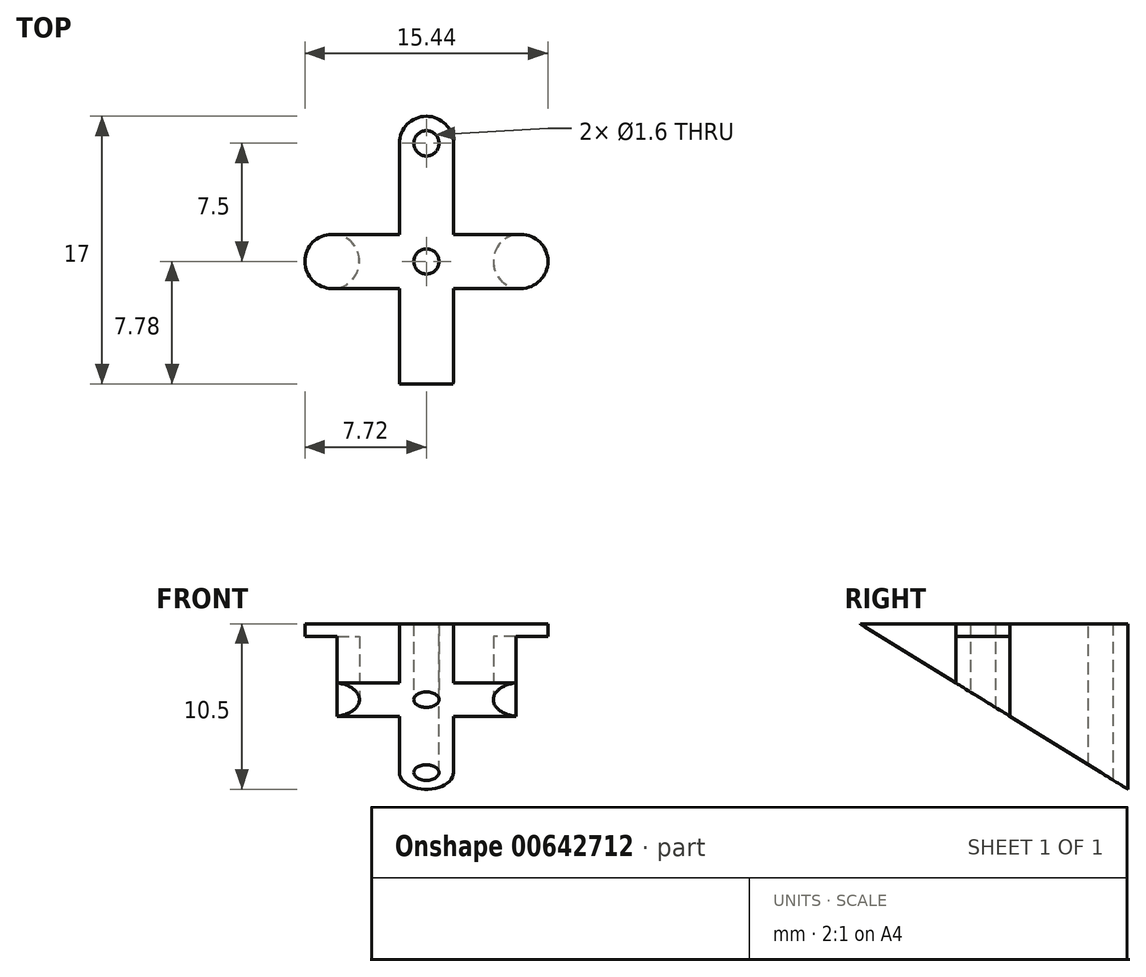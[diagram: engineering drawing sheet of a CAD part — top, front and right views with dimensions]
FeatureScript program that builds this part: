
annotation { "Feature Type Name" : "Feature", "Feature Type Description" : "" }
export const myFeature = defineFeature(function(context is Context, id is Id, definition is map)
    precondition{}
    {
        {
            var Q0;
            Q0=qCreatedBy(makeId("Top.planeOp"),FACE);
            var sketch = newSketch(context, id + "F0", { "sketchPlane" : qUnion([Q0])});
            skLineSegment(sketch, "E0.bottom", {"start": v(6, -1.72) * mm, "end": v(-6, -1.72) * mm});
            skLineSegment(sketch, "E0.top", {"start": v(6, 1.72) * mm, "end": v(-6, 1.72) * mm});
            skLineSegment(sketch, "E0.left", {"start": v(6, -1.72) * mm, "end": v(6, 1.72) * mm});
            skLineSegment(sketch, "E0.right", {"start": v(-6, -1.72) * mm, "end": v(-6, 1.72) * mm});
            skPoint(sketch, "E0.middle", {"position": v(0, 0) * mm});
            skLineSegment(sketch, "E1.bottom", {"start": v(1.72, -7.5) * mm, "end": v(-1.72, -7.5) * mm});
            skLineSegment(sketch, "E1.top", {"start": v(1.72, 7.5) * mm, "end": v(-1.72, 7.5) * mm});
            skLineSegment(sketch, "E1.left", {"start": v(1.72, -7.5) * mm, "end": v(1.72, 7.5) * mm});
            skLineSegment(sketch, "E1.right", {"start": v(-1.72, -7.5) * mm, "end": v(-1.72, 7.5) * mm});
            skArc(sketch, "E2", {"start": v(1.72, 7.5) * mm, "mid": v(0, 9.22) * mm, "end": v(-1.72, 7.5) * mm});
            skArc(sketch, "E3", {"start": v(6, -1.72) * mm, "mid": v(7.72, 0) * mm, "end": v(6, 1.72) * mm});
            skArc(sketch, "E4", {"start": v(-1.72, -7.5) * mm, "mid": v(0, -9.22) * mm, "end": v(1.72, -7.5) * mm});
            skArc(sketch, "E5", {"start": v(-6, 1.72) * mm, "mid": v(-7.72, 0) * mm, "end": v(-6, -1.72) * mm});
            skSolve(sketch);
        }
        {
            var Q0;
            Q0 = qSketchRegion(id + "F0", true);
            extrude(context, id + "F1", {"entities" : qUnion([Q0]), "depth" : 12 * mm, "offsetDistance" : 25 * mm});
        }
        {
            var Q0;
            Q0=qCreatedBy(makeId("Right.planeOp"),FACE);
            var sketch = newSketch(context, id + "F2", { "sketchPlane" : qUnion([Q0])});
            skLineSegment(sketch, "E6.0.0", {"start": v(7.5, 0) * mm, "end": v(9.22, 0) * mm, "construction": true});
            skLineSegment(sketch, "E6.0.1", {"start": v(7.5, 0) * mm, "end": v(7.5, 12) * mm});
            skLineSegment(sketch, "E6.0.2", {"start": v(7.5, 12) * mm, "end": v(9.22, 12) * mm, "construction": true});
            skLineSegment(sketch, "E6.0.3", {"start": v(7.5, 12) * mm, "end": v(7.5, 0) * mm, "construction": true});
            skLineSegment(sketch, "E7.0.0", {"start": v(-7.5, 0) * mm, "end": v(-9.22, 0) * mm, "construction": true});
            skLineSegment(sketch, "E7.0.1", {"start": v(-7.5, 0) * mm, "end": v(-7.5, 12) * mm});
            skLineSegment(sketch, "E7.0.2", {"start": v(-7.5, 12) * mm, "end": v(-9.22, 12) * mm, "construction": true});
            skLineSegment(sketch, "E7.0.3", {"start": v(-7.5, 12) * mm, "end": v(-7.5, 0) * mm});
            skLineSegment(sketch, "E8", {"start": v(9.22, 0) * mm, "end": v(-9.22, 11.39) * mm});
            skLineSegment(sketch, "E9", {"start": v(-9.22, 11.39) * mm, "end": v(-9.22, 0) * mm});
            skLineSegment(sketch, "E10", {"start": v(9.22, 0) * mm, "end": v(-9.22, 0) * mm});
            skSolve(sketch);
        }
        {
            var Q0;
            Q0 = qSketchRegion(id + "F2", true);
            extrude(context, id + "F3", {"entities" : qUnion([Q0]), "operationType" : NewBodyOperationType.REMOVE, "oppositeDirection" : true, "depth" : 25 * mm, "offsetDistance" : 25 * mm, "hasSecondDirection" : true, "secondDirectionOppositeDirection" : false, "secondDirectionDepth" : 25 * mm});
        }
        {
            var Q0;
            Q0=qCreatedBy(makeId("Top.planeOp"),FACE);
            var sketch = newSketch(context, id + "F4", { "sketchPlane" : qUnion([Q0])});
            skLineSegment(sketch, "E11.0", {"start": v(-1.72, 1.72) * mm, "end": v(-1.72, 7.5) * mm, "construction": true});
            skLineSegment(sketch, "E12.0", {"start": v(1.72, 1.72) * mm, "end": v(1.72, 7.5) * mm, "construction": true});
            skPoint(sketch, "E13.0", {"position": v(3.86, 1.72) * mm});
            skLineSegment(sketch, "E14.0", {"start": v(6, 1.72) * mm, "end": v(1.72, 1.72) * mm, "construction": true});
            skLineSegment(sketch, "E15.0", {"start": v(6, -1.72) * mm, "end": v(1.72, -1.72) * mm, "construction": true});
            skLineSegment(sketch, "E16.0", {"start": v(1.72, -7.5) * mm, "end": v(1.72, -1.72) * mm, "construction": true});
            skLineSegment(sketch, "E17.0", {"start": v(-1.72, -7.5) * mm, "end": v(-1.72, -1.72) * mm, "construction": true});
            skPoint(sketch, "E18.0", {"position": v(-3.86, -1.72) * mm});
            skLineSegment(sketch, "E19.0", {"start": v(-1.72, -1.72) * mm, "end": v(-6, -1.72) * mm, "construction": true});
            skPoint(sketch, "E20.0", {"position": v(-3.86, 1.72) * mm});
            skLineSegment(sketch, "E21.0", {"start": v(-1.72, 1.72) * mm, "end": v(-6, 1.72) * mm, "construction": true});
            skCircle(sketch, "E22", {"center": v(6, 0) * mm, "radius": 1.75 * mm});
            skCircle(sketch, "E23", {"center": v(-6, 0) * mm, "radius": 1.75 * mm});
            skSolve(sketch);
        }
        {
            var Q0;
            Q0=qCreatedBy(makeId("Top.planeOp"),FACE);
            var sketch = newSketch(context, id + "F5", { "sketchPlane" : qUnion([Q0])});
            skCircle(sketch, "E24", {"center": v(0, 0) * mm, "radius": 0.8 * mm});
            skSolve(sketch);
        }
        {
            var Q0;
            Q0 = qSketchRegion(id + "F5", true);
            extrude(context, id + "F6", {"entities" : qUnion([Q0]), "operationType" : NewBodyOperationType.REMOVE, "depth" : 55 * mm, "offsetDistance" : 25 * mm});
        }
        {
            var Q0;
            Q0=makeQuery(id+"F1.opExtrude","CAP_FACE",FACE,{"disambiguationData":[OSD([sQuery(id+"F0.wireOp",EDGE,"E0.bottom"),sQuery(id+"F0.wireOp",EDGE,"E0.top"),sQuery(id+"F0.wireOp",EDGE,"E1.left"),sQuery(id+"F0.wireOp",EDGE,"E1.right"),sQuery(id+"F0.wireOp",EDGE,"E2"),sQuery(id+"F0.wireOp",EDGE,"E3"),sQuery(id+"F0.wireOp",EDGE,"E4"),sQuery(id+"F0.wireOp",EDGE,"E5")])],"isStart":false});
            var sketch = newSketch(context, id + "F7", { "sketchPlane" : qUnion([Q0])});
            skLineSegment(sketch, "E25.bottom", {"start": v(15.32, -11.97) * mm, "end": v(-15.32, -11.97) * mm});
            skLineSegment(sketch, "E25.top", {"start": v(15.32, 11.97) * mm, "end": v(-15.32, 11.97) * mm});
            skLineSegment(sketch, "E25.left", {"start": v(15.32, -11.97) * mm, "end": v(15.32, 11.97) * mm});
            skLineSegment(sketch, "E25.right", {"start": v(-15.32, -11.97) * mm, "end": v(-15.32, 11.97) * mm});
            skPoint(sketch, "E25.middle", {"position": v(0, 0) * mm});
            skSolve(sketch);
        }
        {
            var Q0;
            Q0 = qSketchRegion(id + "F7", true);
            extrude(context, id + "F8", {"entities" : qUnion([Q0]), "operationType" : NewBodyOperationType.REMOVE, "oppositeDirection" : true, "depth" : 1.5 * mm, "offsetDistance" : 25 * mm});
        }
        {
            var Q0;
            Q0=makeQuery(id+"F8.boolean.opBoolean","COPY",FACE,{"derivedFrom":makeQuery(id+"F8.opExtrude","CAP_FACE",FACE,{"disambiguationData":[OSD([sQuery(id+"F7.wireOp",EDGE,"E25.bottom"),sQuery(id+"F7.wireOp",EDGE,"E25.top"),sQuery(id+"F7.wireOp",EDGE,"E25.left"),sQuery(id+"F7.wireOp",EDGE,"E25.right")])],"isStart":false})});
            var sketch = newSketch(context, id + "F9", { "sketchPlane" : qUnion([Q0])});
            skLineSegment(sketch, "E26.0", {"start": v(-1.72, 1.72) * mm, "end": v(-1.72, 7.5) * mm, "construction": true});
            skCircle(sketch, "E27", {"center": v(0, 7.5) * mm, "radius": 0.8 * mm});
            skSolve(sketch);
        }
        {
            var Q0;
            Q0 = qSketchRegion(id + "F9", true);
            extrude(context, id + "F10", {"entities" : qUnion([Q0]), "operationType" : NewBodyOperationType.REMOVE, "endBound" : BoundingType.THROUGH_ALL, "oppositeDirection" : true, "depth" : 25 * mm, "offsetDistance" : 25 * mm});
        }
        {
            var Q0;
            Q0=makeQuery(id+"F3.boolean.opBoolean","COPY",FACE,{"derivedFrom":makeQuery(id+"F3.opExtrude","SWEPT_FACE",FACE,{"disambiguationData":[OSD([sQuery(id+"F2.wireOp",EDGE,"E8")])]})});
            cPlane(context, id + "F11", {"entities" : qUnion([Q0]), "cplaneType" : CPlaneType.OFFSET, "offset" : 2 * mm, "oppositeDirection" : true, "width" : 150 * mm, "height" : 150 * mm});
        }
        {
            var Q0;
            Q0 = qSketchRegion(id + "F4", true);
            extrude(context, id + "F12", {"entities" : qUnion([Q0]), "operationType" : NewBodyOperationType.REMOVE, "depth" : 9.7 * mm, "offsetDistance" : 25 * mm});
        }
    });
